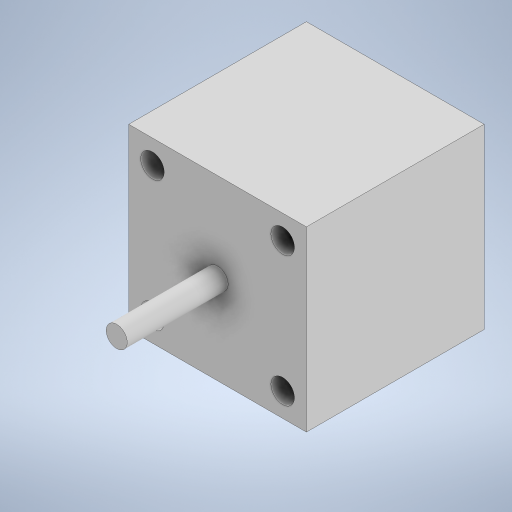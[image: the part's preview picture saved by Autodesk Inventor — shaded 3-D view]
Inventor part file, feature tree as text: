
AUTODESK INVENTOR PART (.ipt)
format: ipt  version: 2024 (Build 280153000, 153)  size: 227,840 bytes
history: native  units: in
note: dims shown in document units (in); Inventor stores cm internally (conversion verified against a paired STEP export)
features: extrude x3, sketch x3, projected_geometry x2
ambient origin geometry x8: Origin, YZ Plane, XZ Plane, XY Plane, X Axis, Y Axis, Z Axis, Center Point
bodies: Solid1 (feature_tree)
feature tree (8):
  extrude  "Extrusion1"  Depth=1.665in
  extrude  "Extrusion2"  Depth=1.665in
  extrude  "Extrusion3"  Depth=0.945in
  sketch  "Sketch1"  dims[d0=1.665in d1=1.665in]
  sketch  "Sketch2"  dims[d2=1.665in d3=0.0in d4=1.22in]
  projected_geometry  "Projected Loop1"
  sketch  "Sketch3"  dims[d5=1.22in d8=0.22in d9=0.22in d10=0.22in d11=0.22in d12=2.71in d13=0.0in d14=0.197in d15=0.945in d16=0.0in]
  projected_geometry  "Projected Loop2"
